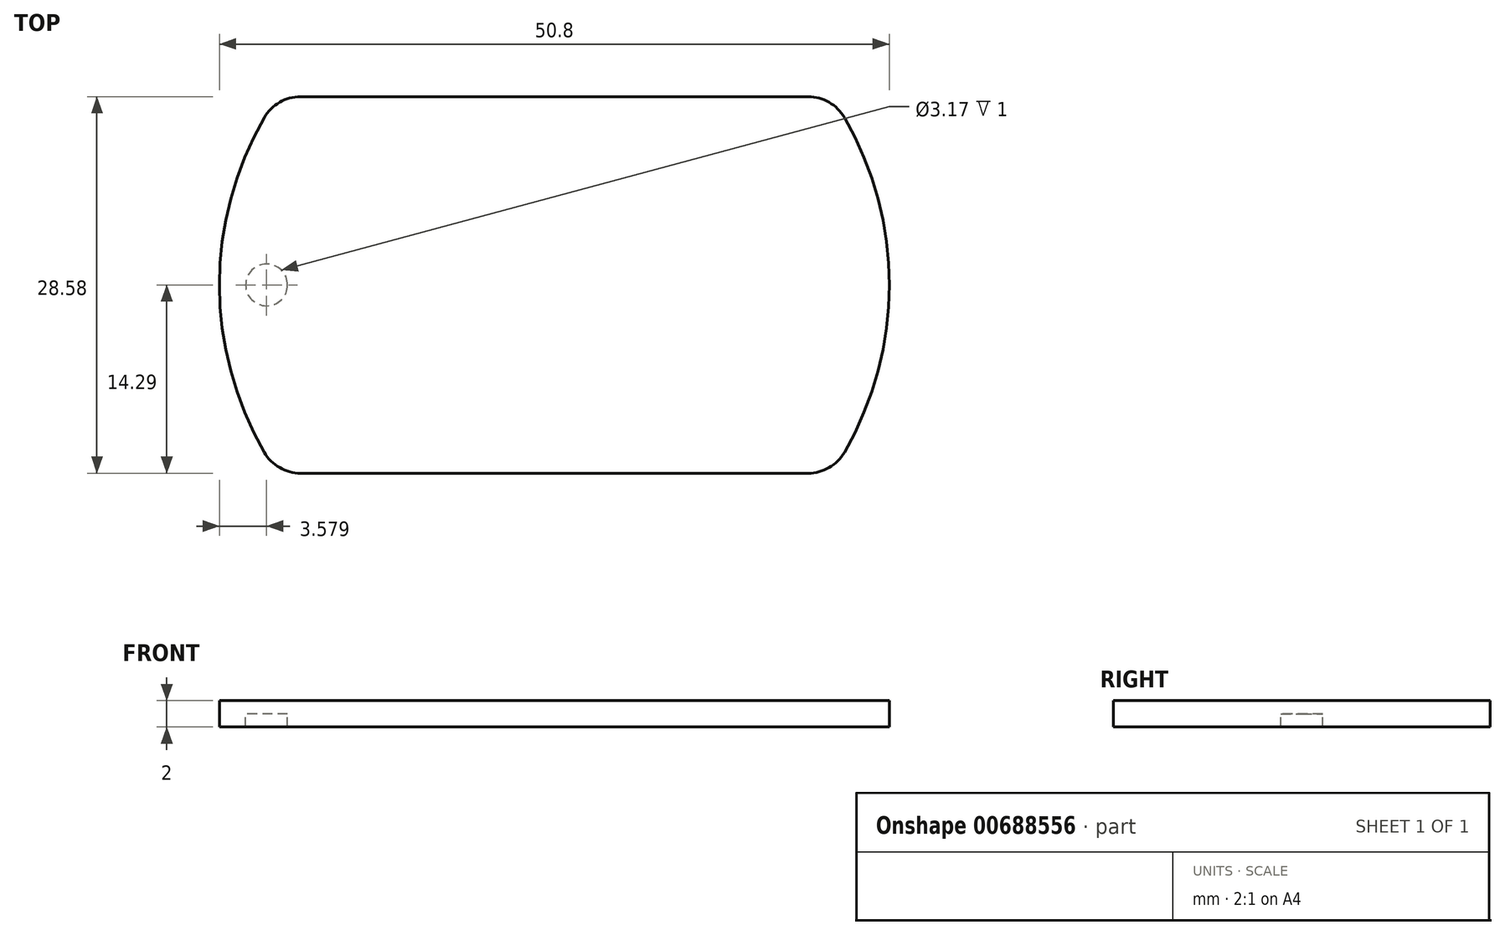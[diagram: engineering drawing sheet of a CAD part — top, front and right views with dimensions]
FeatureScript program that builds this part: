
annotation { "Feature Type Name" : "Feature", "Feature Type Description" : "" }
export const myFeature = defineFeature(function(context is Context, id is Id, definition is map)
    precondition{}
    {
        {
            var Q0;
            Q0=qCreatedBy(makeId("Top.planeOp"),FACE);
            var sketch = newSketch(context, id + "F0", { "sketchPlane" : qUnion([Q0])});
            skArc(sketch, "E0", {"start": v(-22, 12.7) * mm, "mid": v(-25.4, 0) * mm, "end": v(-22, -12.7) * mm});
            skLineSegment(sketch, "E1.top", {"start": v(-19.25, -14.29) * mm, "end": v(19.25, -14.29) * mm});
            skArc(sketch, "E2.trimOffspring", {"start": v(22, -12.7) * mm, "mid": v(25.4, 0) * mm, "end": v(22, 12.7) * mm});
            skLineSegment(sketch, "E3", {"start": v(-19.25, 14.29) * mm, "end": v(19.25, 14.29) * mm});
            skPoint(sketch, "E4.visualSharp", {"position": v(-21, 14.29) * mm});
            skArc(sketch, "E4.filletArc", {"start": v(-19.25, 14.29) * mm, "mid": v(-20.83, 13.86) * mm, "end": v(-22, 12.7) * mm});
            skPoint(sketch, "E5.visualSharp", {"position": v(21, 14.29) * mm});
            skArc(sketch, "E5.filletArc", {"start": v(22, 12.7) * mm, "mid": v(20.83, 13.86) * mm, "end": v(19.25, 14.29) * mm});
            skPoint(sketch, "E6.visualSharp", {"position": v(21, -14.29) * mm});
            skArc(sketch, "E6.filletArc", {"start": v(19.25, -14.29) * mm, "mid": v(20.83, -13.86) * mm, "end": v(22, -12.7) * mm});
            skPoint(sketch, "E7.visualSharp", {"position": v(-21, -14.29) * mm});
            skArc(sketch, "E7.filletArc", {"start": v(-22, -12.7) * mm, "mid": v(-20.83, -13.86) * mm, "end": v(-19.25, -14.29) * mm});
            skSolve(sketch);
        }
        {
            var Q0;
            Q0=makeQuery(id+"F0.imprint","IMPRINT",FACE,{"disambiguationData":[TD([[makeQuery(id+"F0.imprint","IMPRINT",EDGE,{"derivedFrom":sQuery(id+"F0.wireOp",EDGE,"E0")}),1.0]])]});
            extrude(context, id + "F1", {"entities" : qUnion([Q0]), "depth" : 1 * mm, "offsetDistance" : 25.4 * mm});
        }
        {
            var Q0;
            Q0=makeQuery(id+"F1.opExtrude","CAP_FACE",FACE,{"disambiguationData":[OSD([sQuery(id+"F0.wireOp",EDGE,"E0"),sQuery(id+"F0.wireOp",EDGE,"E1.top"),sQuery(id+"F0.wireOp",EDGE,"E2.trimOffspring"),sQuery(id+"F0.wireOp",EDGE,"E3"),sQuery(id+"F0.wireOp",EDGE,"E4.filletArc"),sQuery(id+"F0.wireOp",EDGE,"E5.filletArc"),sQuery(id+"F0.wireOp",EDGE,"E6.filletArc"),sQuery(id+"F0.wireOp",EDGE,"E7.filletArc")])],"isStart":false});
            var sketch = newSketch(context, id + "F2", { "sketchPlane" : qUnion([Q0])});
            skLineSegment(sketch, "E8.0", {"start": v(-18.66, 13.29) * mm, "end": v(18.66, 13.29) * mm});
            skArc(sketch, "E8.1", {"start": v(-21.45, 11.63) * mm, "mid": v(-24.4, 0) * mm, "end": v(-21.45, -11.63) * mm});
            skLineSegment(sketch, "E8.2", {"start": v(-18.66, -13.29) * mm, "end": v(18.66, -13.29) * mm});
            skArc(sketch, "E8.3", {"start": v(21.45, -11.63) * mm, "mid": v(24.4, 0) * mm, "end": v(21.45, 11.63) * mm});
            skPoint(sketch, "E9.visualSharp", {"position": v(-20.46, 13.29) * mm});
            skArc(sketch, "E9.filletArc", {"start": v(-18.66, 13.29) * mm, "mid": v(-20.29, 12.84) * mm, "end": v(-21.45, 11.63) * mm});
            skPoint(sketch, "E10.visualSharp", {"position": v(20.46, 13.29) * mm});
            skArc(sketch, "E10.filletArc", {"start": v(21.45, 11.63) * mm, "mid": v(20.29, 12.84) * mm, "end": v(18.66, 13.29) * mm});
            skPoint(sketch, "E11.visualSharp", {"position": v(20.46, -13.29) * mm});
            skArc(sketch, "E11.filletArc", {"start": v(18.66, -13.29) * mm, "mid": v(20.29, -12.84) * mm, "end": v(21.45, -11.63) * mm});
            skPoint(sketch, "E12.visualSharp", {"position": v(-20.46, -13.29) * mm});
            skArc(sketch, "E12.filletArc", {"start": v(-21.45, -11.63) * mm, "mid": v(-20.29, -12.84) * mm, "end": v(-18.66, -13.29) * mm});
            skLineSegment(sketch, "E13.0", {"start": v(-19.25, 14.29) * mm, "end": v(19.25, 14.29) * mm});
            skArc(sketch, "E13.1", {"start": v(-22, 12.7) * mm, "mid": v(-25.4, 0) * mm, "end": v(-22, -12.7) * mm});
            skLineSegment(sketch, "E13.2", {"start": v(-19.25, -14.29) * mm, "end": v(19.25, -14.29) * mm});
            skArc(sketch, "E13.3", {"start": v(22, -12.7) * mm, "mid": v(25.4, 0) * mm, "end": v(22, 12.7) * mm});
            skPoint(sketch, "E14.visualSharp", {"position": v(-21, -14.29) * mm});
            skArc(sketch, "E14.filletArc", {"start": v(-22, -12.7) * mm, "mid": v(-20.83, -13.86) * mm, "end": v(-19.25, -14.29) * mm});
            skPoint(sketch, "E15.visualSharp", {"position": v(21, -14.29) * mm});
            skArc(sketch, "E15.filletArc", {"start": v(19.25, -14.29) * mm, "mid": v(20.83, -13.86) * mm, "end": v(22, -12.7) * mm});
            skPoint(sketch, "E16.visualSharp", {"position": v(21, 14.29) * mm});
            skArc(sketch, "E16.filletArc", {"start": v(22, 12.7) * mm, "mid": v(20.83, 13.86) * mm, "end": v(19.25, 14.29) * mm});
            skPoint(sketch, "E17.visualSharp", {"position": v(-21, 14.29) * mm});
            skArc(sketch, "E17.filletArc", {"start": v(-19.25, 14.29) * mm, "mid": v(-20.83, 13.86) * mm, "end": v(-22, 12.7) * mm});
            skSolve(sketch);
        }
        {
            var Q0;
            Q0=makeQuery(id+"F2.imprint","IMPRINT",FACE,{"disambiguationData":[TD([[makeQuery(id+"F2.imprint","IMPRINT",EDGE,{"derivedFrom":sQuery(id+"F2.wireOp",EDGE,"E8.0")}),1.0]])]});
            extrude(context, id + "F3", {"entities" : qUnion([Q0]), "operationType" : NewBodyOperationType.ADD, "depth" : 1 * mm, "offsetDistance" : 25.4 * mm});
        }
        {
            var Q0;
            Q0=makeQuery(id+"F1.opExtrude","CAP_FACE",FACE,{"disambiguationData":[OSD([sQuery(id+"F0.wireOp",EDGE,"E0"),sQuery(id+"F0.wireOp",EDGE,"E1.top"),sQuery(id+"F0.wireOp",EDGE,"E2.trimOffspring"),sQuery(id+"F0.wireOp",EDGE,"E3"),sQuery(id+"F0.wireOp",EDGE,"E4.filletArc"),sQuery(id+"F0.wireOp",EDGE,"E5.filletArc"),sQuery(id+"F0.wireOp",EDGE,"E6.filletArc"),sQuery(id+"F0.wireOp",EDGE,"E7.filletArc")])],"isStart":false});
            var sketch = newSketch(context, id + "F4", { "sketchPlane" : qUnion([Q0])});
            skCircle(sketch, "E18", {"center": v(-21.82, 0) * mm, "radius": 1.59 * mm});
            skSolve(sketch);
        }
        {
            var Q0;
            Q0=makeQuery(id+"F4.imprint","IMPRINT",FACE,{"disambiguationData":[TD([[makeQuery(id+"F4.imprint","IMPRINT",EDGE,{"derivedFrom":sQuery(id+"F4.wireOp",EDGE,"E18")}),1.0]])]});
            extrude(context, id + "F5", {"entities" : qUnion([Q0]), "operationType" : NewBodyOperationType.REMOVE, "oppositeDirection" : true, "depth" : 1 * mm, "offsetDistance" : 25.4 * mm});
        }
        {
            var Q0;
            Q0=makeQuery(id+"F2.imprint","IMPRINT",FACE,{"disambiguationData":[TD([[makeQuery(id+"F2.imprint","IMPRINT",EDGE,{"derivedFrom":sQuery(id+"F2.wireOp",EDGE,"E8.0")}),-1.0]])]});
            var sketch = newSketch(context, id + "F6", { "sketchPlane" : qUnion([Q0])});
            skText(sketch, "E19", { "text": "David", "fontName": "OpenSans-Regular.ttf"});
            skText(sketch, "E20", { "text": "#JellyFam", "fontName": "OpenSans-Regular.ttf"});
            const initialGuessF6  = {"E19": [-0.0152, 0.004, 1, 0, 0.00653], "E20": [-0.01124, -0.0095, 1, 0, 0.0044]};
            skSetInitialGuess(sketch, initialGuessF6);
            skSolve(sketch);
        }
        {
            var Q0;
            Q0 = qSketchRegion(id + "F6", true);
            extrude(context, id + "F7", {"entities" : qUnion([Q0]), "operationType" : NewBodyOperationType.ADD, "depth" : 1 * mm, "offsetDistance" : 25.4 * mm});
        }
        {
            var Q0;
            Q0=makeQuery(id+"F2.imprint","IMPRINT",FACE,{"disambiguationData":[TD([[makeQuery(id+"F2.imprint","IMPRINT",EDGE,{"derivedFrom":sQuery(id+"F2.wireOp",EDGE,"E8.0")}),-1.0]])]});
            var Q1;
            Q1 = qSketchRegion(id + "F6", true);
            extrude(context, id + "F8", {"entities" : qUnion([Q0, Q1]), "operationType" : NewBodyOperationType.ADD, "depth" : 1 * mm, "offsetDistance" : 25.4 * mm});
        }
    });
